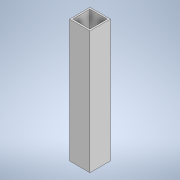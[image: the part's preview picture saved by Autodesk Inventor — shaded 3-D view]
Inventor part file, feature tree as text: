
AUTODESK INVENTOR PART (.ipt)
format: ipt  version: 2022 (Build 260153000, 153)  size: 98,816 bytes
history: native  units: mm
features: extrude x1, sketch x1
ambient origin geometry x8: Origin, YZ Plane, XZ Plane, XY Plane, X Axis, Y Axis, Z Axis, Center Point
bodies: Solid1 (feature_tree)
feature tree (2):
  extrude  "Extrusion1"  Depth=25.4mm
  sketch  "Sketch1"  dims[d0=25.4mm d1=25.4mm d2=2.0mm d3=152.4mm d4=0.0mm]
